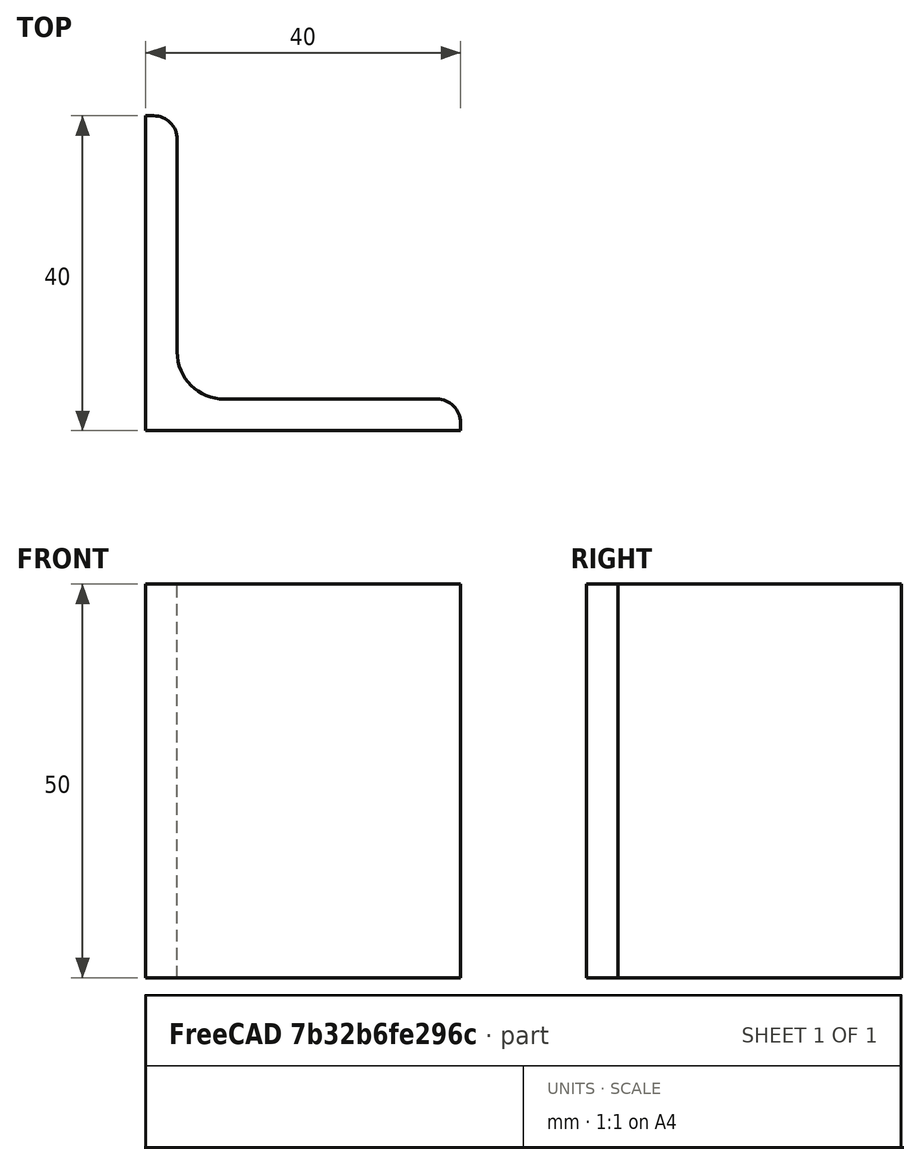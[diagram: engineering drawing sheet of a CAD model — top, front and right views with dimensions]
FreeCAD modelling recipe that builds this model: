
FCSTD DOCUMENT  (FreeCAD 0.15R4671 (Git))
Label: Angle Bar L40x40x4 EN10056 S235JR
License: All rights reserved
LicenseURL: http://en.wikipedia.org/wiki/All_rights_reserved
objects: Sketcher::SketchObject×1, Part::Extrusion×1
note: 2 computed .brp shape members not serialized (recipe doc carries the construction recipe); baked Part::Feature solids carry a one-line shape summary decoded from their .brp

FEATURE [Sketcher::SketchObject] Sketch
  sketch-geometry (9):
    g0: LineSegment StartX=0 StartY=0 StartZ=0 EndX=40 EndY=0 EndZ=0
    g1: LineSegment StartX=40 StartY=0 StartZ=0 EndX=40 EndY=1 EndZ=0
    g2: LineSegment StartX=37 StartY=4 StartZ=0 EndX=10 EndY=4 EndZ=0
    g3: LineSegment StartX=0 StartY=0 StartZ=0 EndX=0 EndY=40 EndZ=0
    g4: LineSegment StartX=0 StartY=40 StartZ=0 EndX=1 EndY=40 EndZ=0
    g5: LineSegment StartX=4 StartY=37 StartZ=0 EndX=4 EndY=10 EndZ=0
    g6: ArcOfCircle CenterX=10 CenterY=10 CenterZ=0 NormalX=0 NormalY=0 NormalZ=1 Radius=6 StartAngle=3.14159 EndAngle=4.71239
    g7: ArcOfCircle CenterX=1 CenterY=37 CenterZ=0 NormalX=0 NormalY=0 NormalZ=1 Radius=3 StartAngle=0 EndAngle=1.5708
    g8: ArcOfCircle CenterX=37 CenterY=1 CenterZ=0 NormalX=0 NormalY=0 NormalZ=1 Radius=3 StartAngle=0 EndAngle=1.5708
  constraints (23):
    c: Coincident(g0,g-1)
    c: Horizontal(g0)
    c: Coincident(g1,g0)
    c: Vertical(g1)
    c: Horizontal(g2)
    c: Coincident(g3,g-1)
    c: Vertical(g3)
    c: Coincident(g4,g3)
    c: Horizontal(g4)
    c: Vertical(g5)
    c: Tangent(g5,g6) = -1.5708
    c: Tangent(g2,g6) = 1.5708
    c: Tangent(g4,g7) = 1.5708
    c: Tangent(g5,g7) = 1.5708
    c: Tangent(g2,g8) = -1.5708
    c: Tangent(g1,g8) = -1.5708
    c: DistanceX(g0) = 40
    c: DistanceY(g3) = 40
    c: DistanceY(g0,g2) = 4
    c: DistanceX(g3,g5) = 4
    c: Radius(g6) = 6
    c: Radius(g8) = 3
    c: Radius(g7) = 3
FEATURE [Part::Extrusion] Extrude  label="Angle Bar L40x40x4 EN10056 S235JR"
  Base = -> Sketch
  Dir = (0,0,50)
  Solid = true
